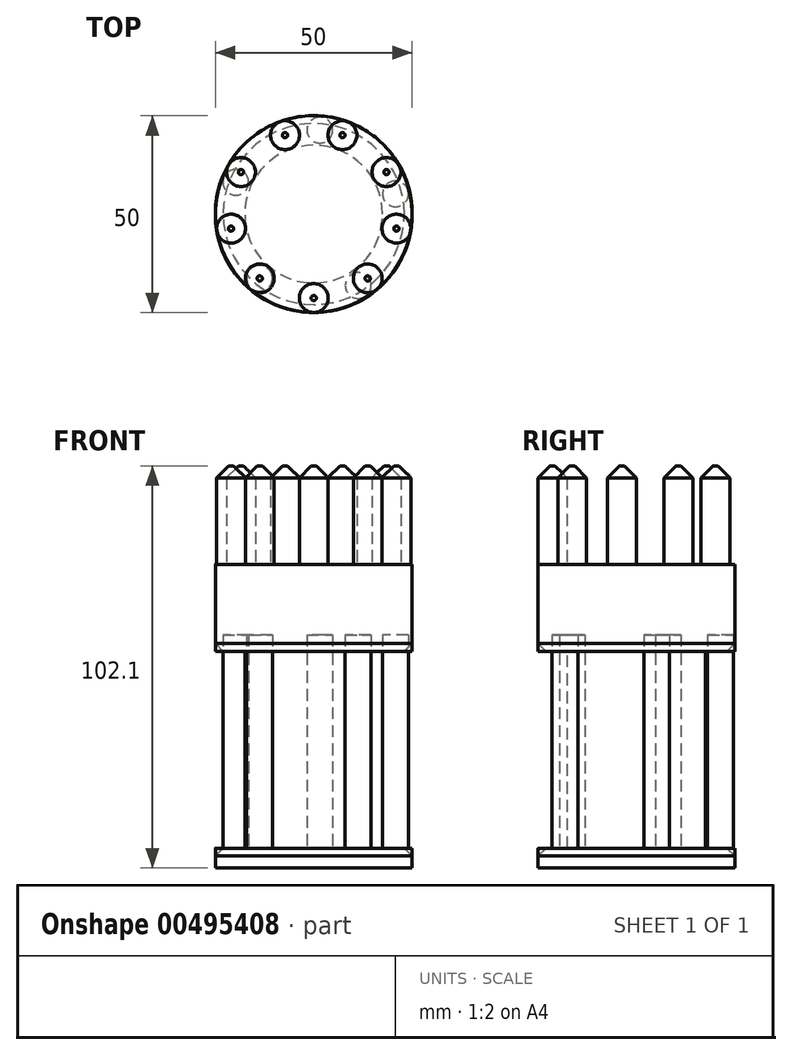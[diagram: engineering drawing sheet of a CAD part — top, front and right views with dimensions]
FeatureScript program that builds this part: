
annotation { "Feature Type Name" : "Feature", "Feature Type Description" : "" }
export const myFeature = defineFeature(function(context is Context, id is Id, definition is map)
    precondition{}
    {
        {
            var Q0;
            Q0=qCreatedBy(makeId("Right.planeOp"),FACE);
            var sketch = newSketch(context, id + "F0", { "sketchPlane" : qUnion([Q0])});
            skLineSegment(sketch, "E0", {"start": v(0, 0) * mm, "end": v(-25, 0) * mm});
            skLineSegment(sketch, "E1", {"start": v(-25, 0) * mm, "end": v(-25, 5) * mm});
            skLineSegment(sketch, "E2", {"start": v(-25, 5) * mm, "end": v(-17.5, 5) * mm});
            skLineSegment(sketch, "E3", {"start": v(-17.5, 5) * mm, "end": v(-17.5, 55) * mm});
            skLineSegment(sketch, "E4", {"start": v(-17.5, 55) * mm, "end": v(-25, 55) * mm});
            skLineSegment(sketch, "E5", {"start": v(-25, 55) * mm, "end": v(-25, 77.1) * mm});
            skLineSegment(sketch, "E6", {"start": v(-25, 77.1) * mm, "end": v(0, 77.1) * mm});
            skLineSegment(sketch, "E7", {"start": v(0, 77.1) * mm, "end": v(0, 0) * mm});
            skLineSegment(sketch, "E8", {"start": v(0, 103.77) * mm, "end": v(0, -21.18) * mm, "construction": true});
            skSolve(sketch);
        }
        {
            var Q0;
            Q0=makeQuery(id+"F0.imprint","IMPRINT",FACE,{"disambiguationData":[TD([[makeQuery(id+"F0.imprint","IMPRINT",EDGE,{"derivedFrom":sQuery(id+"F0.wireOp",EDGE,"E0")}),-1.0]])]});
            var Q1;
            Q1=sQuery(id+"F0.wireOp",EDGE,"E7");
            revolve(context, id + "F1", {"entities" : qUnion([Q0]), "axis" : qUnion([Q1]), "revolveType" : RevolveType.FULL});
        }
        {
            var Q0;
            Q0=makeQuery(id+"F1.opRevolve","SWEPT_FACE",FACE,{"disambiguationData":[OSD([sQuery(id+"F0.wireOp",EDGE,"E6")])]});
            var sketch = newSketch(context, id + "F2", { "sketchPlane" : qUnion([Q0])});
            skCircle(sketch, "E9", {"center": v(0, -21.33) * mm, "radius": 3.67 * mm});
            skSolve(sketch);
        }
        {
            var Q0;
            Q0 = qSketchRegion(id + "F2", true);
            extrude(context, id + "F3", {"entities" : qUnion([Q0]), "operationType" : NewBodyOperationType.ADD, "depth" : 25 * mm});
        }
        {
            var Q0;
            Q0=makeQuery(id+"F1.opRevolve","SWEPT_BODY",BODY,{"disambiguationData":[OSD([sQuery(id+"F0.wireOp",EDGE,"E0"),sQuery(id+"F0.wireOp",EDGE,"E1"),sQuery(id+"F0.wireOp",EDGE,"E2"),sQuery(id+"F0.wireOp",EDGE,"E3"),sQuery(id+"F0.wireOp",EDGE,"E4"),sQuery(id+"F0.wireOp",EDGE,"E5"),sQuery(id+"F0.wireOp",EDGE,"E6"),sQuery(id+"F0.wireOp",EDGE,"E7")])]});
            var Q1;
            Q1=sQuery(id+"F0.wireOp",EDGE,"E8");
            circularPattern(context, id + "F4", {"entities" : qUnion([Q0]), "axis" : qUnion([Q1]), "angle" : 360 * degree, "instanceCount" : 9, "equalSpace" : true});
        }
        {
            var Q0;
            Q0=makeQuery(id+"F1.opRevolve","SWEPT_FACE",FACE,{"disambiguationData":[OSD([sQuery(id+"F0.wireOp",EDGE,"E2")])]});
            var sketch = newSketch(context, id + "F5", { "sketchPlane" : qUnion([Q0])});
            skCircle(sketch, "E10", {"center": v(20.76, 5.12) * mm, "radius": 3.28 * mm});
            skSolve(sketch);
        }
        {
            var Q0;
            Q0=makeQuery(id+"F5.imprint","IMPRINT",FACE,{"disambiguationData":[TD([[makeQuery(id+"F5.imprint","IMPRINT",EDGE,{"derivedFrom":sQuery(id+"F5.wireOp",EDGE,"E10")}),1.0]])]});
            extrude(context, id + "F6", {"entities" : qUnion([Q0]), "depth" : 54.2 * mm});
        }
        {
            var Q0;
            Q0=makeQuery(id+"F6.opExtrude","SWEPT_BODY",BODY,{"disambiguationData":[OSD([sQuery(id+"F5.wireOp",EDGE,"E10")])]});
            var Q1;
            Q1=sQuery(id+"F0.wireOp",EDGE,"E8");
            circularPattern(context, id + "F7", {"entities" : qUnion([Q0]), "axis" : qUnion([Q1]), "angle" : 360 * degree, "instanceCount" : 5, "equalSpace" : true});
        }
        {
            var Q0;
            Q0=makeQuery(id+"F4.opPattern","COPY",EDGE,{"derivedFrom":makeQuery(id+"F3.opExtrude","CAP_EDGE",EDGE,{"disambiguationData":[OSD([sQuery(id+"F2.wireOp",EDGE,"E9")])],"isStart":false}),"instanceName":"2"});
            var Q1;
            Q1=makeQuery(id+"F4.opPattern","COPY",EDGE,{"derivedFrom":makeQuery(id+"F3.opExtrude","CAP_EDGE",EDGE,{"disambiguationData":[OSD([sQuery(id+"F2.wireOp",EDGE,"E9")])],"isStart":false}),"instanceName":"1"});
            var Q2;
            Q2=makeQuery(id+"F3.opExtrude","CAP_EDGE",EDGE,{"disambiguationData":[OSD([sQuery(id+"F2.wireOp",EDGE,"E9")])],"isStart":false});
            var Q3;
            Q3=makeQuery(id+"F4.opPattern","COPY",EDGE,{"derivedFrom":makeQuery(id+"F3.opExtrude","CAP_EDGE",EDGE,{"disambiguationData":[OSD([sQuery(id+"F2.wireOp",EDGE,"E9")])],"isStart":false}),"instanceName":"8"});
            var Q4;
            Q4=makeQuery(id+"F4.opPattern","COPY",EDGE,{"derivedFrom":makeQuery(id+"F3.opExtrude","CAP_EDGE",EDGE,{"disambiguationData":[OSD([sQuery(id+"F2.wireOp",EDGE,"E9")])],"isStart":false}),"instanceName":"7"});
            var Q5;
            Q5=makeQuery(id+"F4.opPattern","COPY",EDGE,{"derivedFrom":makeQuery(id+"F3.opExtrude","CAP_EDGE",EDGE,{"disambiguationData":[OSD([sQuery(id+"F2.wireOp",EDGE,"E9")])],"isStart":false}),"instanceName":"6"});
            var Q6;
            Q6=makeQuery(id+"F4.opPattern","COPY",EDGE,{"derivedFrom":makeQuery(id+"F3.opExtrude","CAP_EDGE",EDGE,{"disambiguationData":[OSD([sQuery(id+"F2.wireOp",EDGE,"E9")])],"isStart":false}),"instanceName":"5"});
            var Q7;
            Q7=makeQuery(id+"F4.opPattern","COPY",EDGE,{"derivedFrom":makeQuery(id+"F3.opExtrude","CAP_EDGE",EDGE,{"disambiguationData":[OSD([sQuery(id+"F2.wireOp",EDGE,"E9")])],"isStart":false}),"instanceName":"4"});
            var Q8;
            Q8=makeQuery(id+"F4.opPattern","COPY",EDGE,{"derivedFrom":makeQuery(id+"F3.opExtrude","CAP_EDGE",EDGE,{"disambiguationData":[OSD([sQuery(id+"F2.wireOp",EDGE,"E9")])],"isStart":false}),"instanceName":"3"});
            chamfer(context, id + "F8", {"entities" : qUnion([Q0, Q1, Q2, Q3, Q4, Q5, Q6, Q7, Q8]), "width" : 3 * mm, "tangentPropagation" : true});
        }
        {
            var Q0;
            Q0=makeQuery(id+"F1.opRevolve","SWEPT_EDGE",EDGE,{"disambiguationData":[OSD([sQuery(id+"F0.wireOp",EDGE,"E4"),sQuery(id+"F0.wireOp",EDGE,"E5")])]});
            chamfer(context, id + "F9", {"entities" : qUnion([Q0]), "width" : 2 * mm, "tangentPropagation" : true});
        }
        {
            var Q0;
            Q0=makeQuery(id+"F1.opRevolve","SWEPT_EDGE",EDGE,{"disambiguationData":[OSD([sQuery(id+"F0.wireOp",EDGE,"E1"),sQuery(id+"F0.wireOp",EDGE,"E2")])]});
            chamfer(context, id + "F10", {"entities" : qUnion([Q0]), "width" : 2 * mm, "tangentPropagation" : true});
        }
    });
